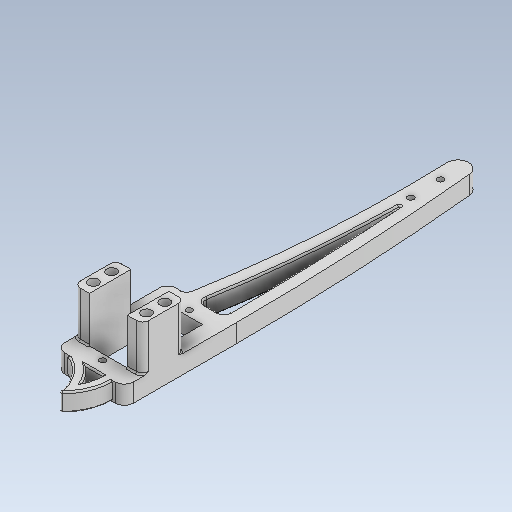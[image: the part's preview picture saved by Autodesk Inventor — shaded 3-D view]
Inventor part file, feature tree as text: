
AUTODESK INVENTOR PART (.ipt)
format: ipt  version: 2020.3 (Build 243373000, 373)  size: 275,456 bytes
history: native  units: mm
features: other x3, sketch x2
ambient origin geometry x8: Origin, YZ Plane, XZ Plane, XY Plane, X Axis, Y Axis, Z Axis, Center Point
bodies: Solid1 (feature_tree)
feature tree (5):
  other  "LegEnd_Right_v1.ipt"
  other  "Solid1::LegEnd_Right_v1.ipt"
  other  "TaggingFeature1"
  sketch  "Sketch1"  dims[d0=10.0mm]
  sketch  "Sketch3"
